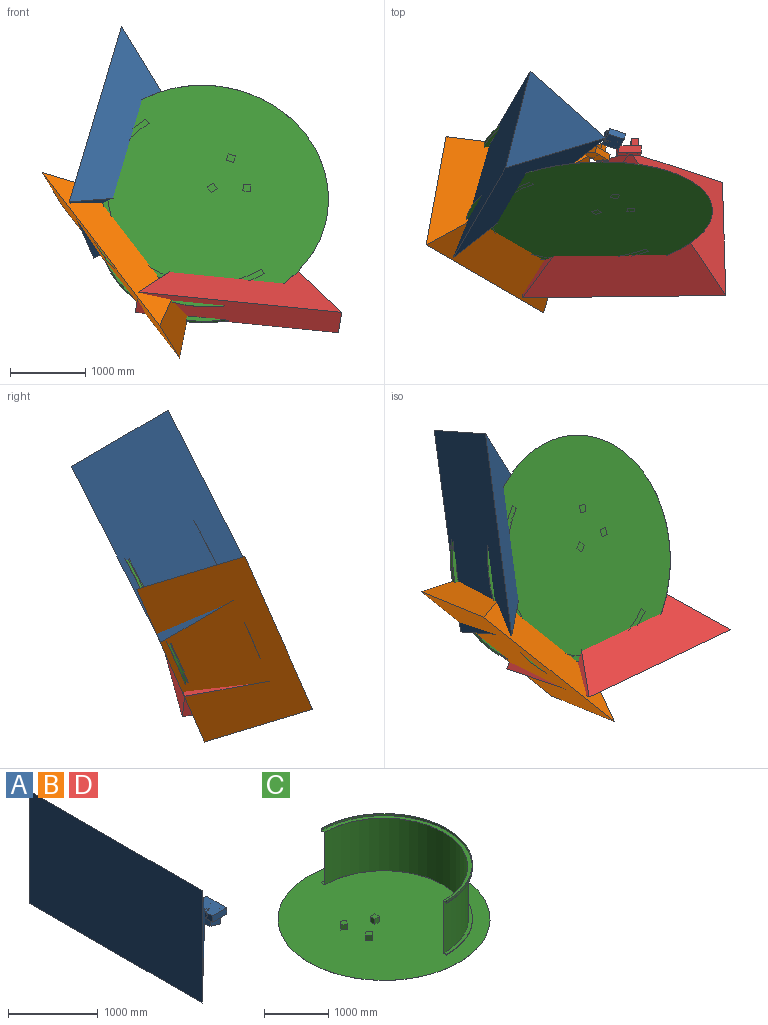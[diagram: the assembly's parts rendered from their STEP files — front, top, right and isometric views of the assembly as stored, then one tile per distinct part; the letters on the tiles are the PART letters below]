
ASSEMBLY  parts=4 mates=9
PART A: 23 faces, bbox 1618.5x2721.1x1856.4 mm
  f0: plane 2721.09x1398mm, normal (-0.12,0,-0.99), area 1918482.9mm2, adj f2,f3,f4,f5
  f1: plane 2721.09x1696.55mm, normal (0.77,0,0.64), area 2995210.2mm2, adj f2,f3,f4,f5
  f2: plane 1698.74x1398mm, normal (0.7,-0.72,0), area 1494026.7mm2, adj f0,f1,f4,f5
  f3: plane 1698.74x1398mm, normal (0.7,0.72,0), area 1494026.7mm2, adj f0,f1,f4,f5
  f4: plane 2721.09x1530.61mm, normal (-1,0,0), area 4164931.3mm2, adj f0,f1,f2,f3
  f5: plane 82.36x82.36mm, normal (-1,0,0), area 5319.1mm2, adj f0,f1,f2,f3,f17
  f6: plane 223.5x87.83mm, normal (0,1,0), area 19630mm2, adj f7,f12,f13,f14
  f7: plane 314.1x92.86mm, normal (-1,0,0), area 21942.5mm2, adj f6,f8,f13,f14,f15,f17
  f8: plane 223.5x87.83mm, normal (0,-1,0), area 19630mm2, adj f7,f12,f13,f14
  f9: cylinder r=2mm len=87.83mm, axis (0,0,-1), area 1103.7mm2, adj f13,f14
  f10: cylinder r=2mm len=87.83mm, axis (0,0,-1), area 1103.7mm2, adj f13,f14
  f11: cylinder r=2mm len=87.83mm, axis (0,0,-1), area 1103.7mm2, adj f13,f14
  f12: plane 314.1x87.83mm, normal (1,0,0), area 27587.4mm2, adj f6,f8,f13,f14
  f13: plane 314.1x223.5mm, normal (0,0,1), area 68098mm2, adj f6,f7,f8,f9,f10,f11,f12,f15
  f14: plane 314.1x223.5mm, normal (0,0,-1), area 55163.7mm2, adj f6,f7,f8,f9,f10,f11,f12,f18
  f15: cylinder r=44.91mm len=50mm, axis (-1,0,0), area 2146.5mm2, adj f7,f13,f16
  f16: plane 41.31x5.03mm, normal (1,0,0), area 140.2mm2, adj f13,f15
  f17: cone r=42.91mm half-angle=30deg, axis (-1,0,0), area 915.2mm2, adj f5,f7
  f18: plane 100x61.43mm, normal (-0.96,0,0.28), area 6390.8mm2, adj f14,f19,f21,f22
  f19: plane 167.62x100mm, normal (-0.28,0,-0.96), area 17437mm2, adj f18,f20,f21,f22
  f20: plane 109.49x100mm, normal (1,0,0), area 10949.5mm2, adj f14,f19,f21,f22
  f21: plane 167.62x109.49mm, normal (0,-1,0), area 13783.9mm2, adj f14,f18,f19,f20
  f22: plane 167.62x109.49mm, normal (0,1,0), area 13783.9mm2, adj f14,f18,f19,f20
PART B: same geometry as A
PART C: 29 faces, bbox 3291.5x3291.5x1037 mm
  f0: plane 3291.51x3291.51mm, normal (0,0,1), area 8163889.3mm2, adj f1,f2,f10,f11,f12,f14,f15,f16
  f1: cylinder r=1300mm len=2600mm, axis (0,0,-1), area 4084070.4mm2, adj f0,f9,f10,f11
  f2: cylinder r=1375mm len=2750mm, axis (0,0,-1), area 56156mm2, adj f0,f3,f10,f11
  f3: plane 2750x1375mm, normal (0,0,1), area 261782.6mm2, adj f2,f4,f10,f11
  f4: cylinder r=1313mm len=2626mm, axis (0,0,-1), area 4017663.5mm2, adj f3,f5,f10,f11
  f5: plane 2750x1375mm, normal (0,0,-1), area 261782.6mm2, adj f4,f6,f10,f11
  f6: cylinder r=1375mm len=2750mm, axis (0,0,-1), area 207345.1mm2, adj f5,f7,f10,f11
  f7: plane 2750x1375mm, normal (0,0,1), area 25861.6mm2, adj f6,f8,f10,f11
  f8: cylinder r=1369mm len=2738mm, axis (0,0,-1), area 150529.4mm2, adj f7,f9,f10,f11
  f9: plane 2738x1369mm, normal (0,0,1), area 289279.4mm2, adj f1,f8,f10,f11
  f10: plane 1035x75mm, normal (-1,0,0), area 14822mm2, adj f0,f1,f2,f3,f4,f5,f6,f7
  f11: plane 1035x75mm, normal (-1,0,0), area 14822mm2, adj f0,f1,f2,f3,f4,f5,f6,f7
  f12: cylinder r=1645.75mm len=3291.51mm, axis (0,0,1), area 20681.2mm2, adj f0,f13
  f13: plane 3291.51x3291.51mm, normal (0,0,-1), area 8509030.3mm2, adj f12
  f14: plane 100x100mm, normal (-1,0,0), area 10000mm2, adj f0,f15,f17,f18
  f15: plane 100x100mm, normal (0,-1,0), area 10000mm2, adj f0,f14,f16,f18
  f16: plane 100x100mm, normal (1,0,0), area 10000mm2, adj f0,f15,f17,f18
  f17: plane 100x100mm, normal (0,1,0), area 10000mm2, adj f0,f14,f16,f18
  f18: plane 100x100mm, normal (0,0,1), area 10000mm2, adj f14,f15,f16,f17
  f19: plane 100x76.6mm, normal (0.77,-0.64,0), area 10000mm2, adj f0,f20,f22,f23
  f20: plane 100x76.6mm, normal (0.64,0.77,0), area 10000mm2, adj f0,f19,f21,f23
  f21: plane 100x76.6mm, normal (-0.77,0.64,0), area 10000mm2, adj f0,f20,f22,f23
  f22: plane 100x76.6mm, normal (-0.64,-0.77,0), area 10000mm2, adj f0,f19,f21,f23
  f23: plane 140.88x140.88mm, normal (0,0,1), area 10000mm2, adj f19,f20,f21,f22
  f24: plane 100x76.6mm, normal (-0.64,0.77,0), area 10000mm2, adj f0,f25,f27,f28
  f25: plane 100x76.6mm, normal (-0.77,-0.64,0), area 10000mm2, adj f0,f24,f26,f28
  f26: plane 100x76.6mm, normal (0.64,-0.77,0), area 10000mm2, adj f0,f25,f27,f28
  f27: plane 100x76.6mm, normal (0.77,0.64,0), area 10000mm2, adj f0,f24,f26,f28
  f28: plane 140.88x140.88mm, normal (0,0,1), area 10000mm2, adj f24,f25,f26,f27
PART D: same geometry as A
PLACE A rot(axis=(0.95,-0.05,-0.31),64.1deg) t=(-2901.73,2116.38,-1001.51)mm
PLACE B rot(axis=(0.86,-0.39,0.31),78deg) t=(-3099,1890.32,-1438.29)mm
PLACE C rot(axis=(-0.27,0.81,0.52),164.2deg) t=(-3121.39,1066.87,-1090.37)mm fixed
PLACE D rot(axis=(0.58,-0.51,0.63),111.7deg) t=(-2570.28,1925.29,-1432.44)mm
MATE planar A.f19 <-> C.f9  axis (-0.05,0.9,-0.44) through (-2823.58,2186.54,-1118.34)mm
MATE planar A.f18 <-> C.f20  axis (-0.97,0.07,0.25) through (-2906,2163.59,-1082.24)mm
MATE planar C.f15 <-> B.f22  axis (0.58,-0.33,-0.75) through (-3001.68,1155.72,-1037.69)mm
MATE planar B.f18 <-> C.f16  axis (-0.82,-0.29,-0.5) through (-3063.7,1947.6,-1503.4)mm
MATE planar D.f22 <-> C.f25  axis (-0.99,-0.01,0.1) through (-2575.16,2029.77,-1468.98)mm
MATE planar A.f22 <-> C.f19  axis (0.26,0.44,0.86) through (-2808.92,2170.63,-1056.59)mm
MATE planar D.f19 <-> C.f9  axis (-0.05,0.9,-0.44) through (-2518.08,2068.94,-1396.12)mm
MATE planar D.f18 <-> C.f26  axis (-0.08,-0.44,-0.89) through (-2523.67,2001.7,-1459.91)mm
MATE planar C.f9 <-> B.f19  axis (-0.05,0.9,-0.44) through (-3869.41,1714.11,-1952.71)mm
